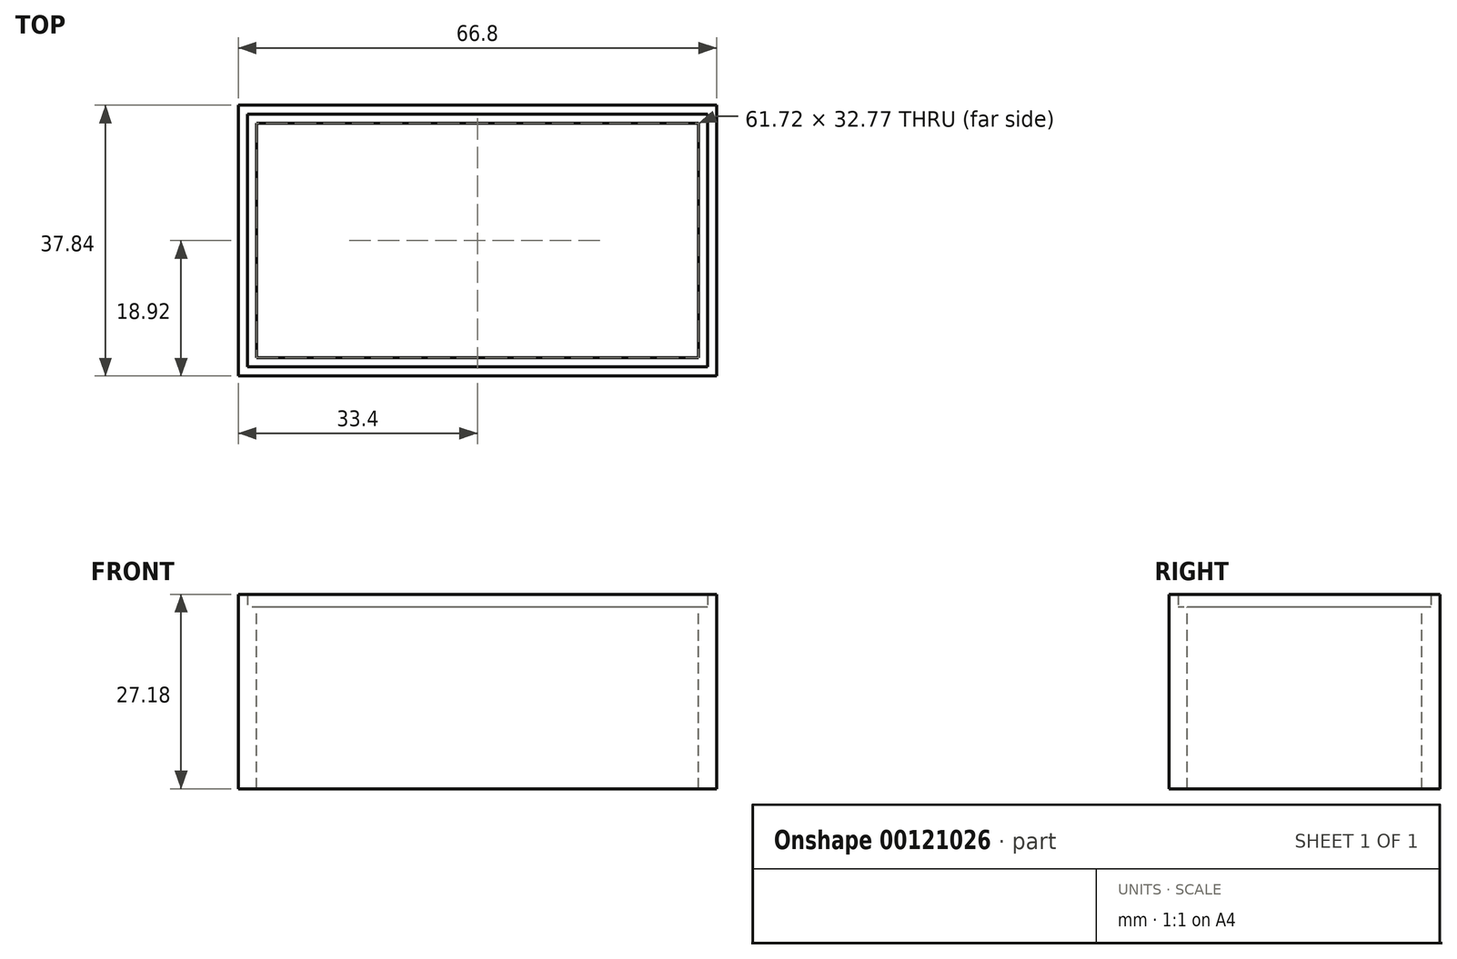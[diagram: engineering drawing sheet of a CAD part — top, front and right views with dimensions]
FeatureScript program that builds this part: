
annotation { "Feature Type Name" : "Feature", "Feature Type Description" : "" }
export const myFeature = defineFeature(function(context is Context, id is Id, definition is map)
    precondition{}
    {
        {
            var Q0;
            Q0=qCreatedBy(makeId("Top.planeOp"),FACE);
            var sketch = newSketch(context, id + "F0", { "sketchPlane" : qUnion([Q0])});
            skLineSegment(sketch, "E0.bottom", {"start": v(32.13, 17.65) * mm, "end": v(-32.13, 17.65) * mm});
            skLineSegment(sketch, "E0.top", {"start": v(32.13, -17.65) * mm, "end": v(-32.13, -17.65) * mm});
            skLineSegment(sketch, "E0.left", {"start": v(32.13, 17.65) * mm, "end": v(32.13, -17.65) * mm});
            skLineSegment(sketch, "E0.right", {"start": v(-32.13, 17.65) * mm, "end": v(-32.13, -17.65) * mm});
            skPoint(sketch, "E0.middle", {"position": v(0, 0) * mm});
            skLineSegment(sketch, "E1.0", {"start": v(30.86, -16.38) * mm, "end": v(-30.86, -16.38) * mm});
            skLineSegment(sketch, "E1.1", {"start": v(30.86, 16.38) * mm, "end": v(30.86, -16.38) * mm});
            skLineSegment(sketch, "E1.2", {"start": v(30.86, 16.38) * mm, "end": v(-30.86, 16.38) * mm});
            skLineSegment(sketch, "E1.3", {"start": v(-30.86, 16.38) * mm, "end": v(-30.86, -16.38) * mm});
            skSolve(sketch);
        }
        {
            var Q0;
            Q0 = qSketchRegion(id + "F0", true);
            extrude(context, id + "F1", {"entities" : qUnion([Q0]), "oppositeDirection" : true, "depth" : 25.4 * mm});
        }
        {
            var Q0;
            Q0=qCreatedBy(makeId("Top.planeOp"),FACE);
            var sketch = newSketch(context, id + "F2", { "sketchPlane" : qUnion([Q0])});
            skLineSegment(sketch, "E2.0", {"start": v(33.4, 18.92) * mm, "end": v(-33.4, 18.92) * mm});
            skLineSegment(sketch, "E2.1", {"start": v(33.4, 18.92) * mm, "end": v(33.4, -18.92) * mm});
            skLineSegment(sketch, "E2.2", {"start": v(33.4, -18.92) * mm, "end": v(-33.4, -18.92) * mm});
            skLineSegment(sketch, "E2.3", {"start": v(-33.4, 18.92) * mm, "end": v(-33.4, -18.92) * mm});
            skLineSegment(sketch, "E3.0", {"start": v(-32.13, 17.65) * mm, "end": v(-32.13, -17.65) * mm});
            skLineSegment(sketch, "E3.1", {"start": v(32.13, -17.65) * mm, "end": v(-32.13, -17.65) * mm});
            skLineSegment(sketch, "E3.2", {"start": v(32.13, 17.65) * mm, "end": v(32.13, -17.65) * mm});
            skLineSegment(sketch, "E3.3", {"start": v(32.13, 17.65) * mm, "end": v(-32.13, 17.65) * mm});
            skSolve(sketch);
        }
        {
            var Q0;
            Q0 = qSketchRegion(id + "F2", true);
            var Q1;
            Q1=makeQuery(id+"F1.opExtrude","CAP_FACE",FACE,{"disambiguationData":[OSD([sQuery(id+"F0.wireOp",EDGE,"E0.bottom"),sQuery(id+"F0.wireOp",EDGE,"E0.top"),sQuery(id+"F0.wireOp",EDGE,"E0.left"),sQuery(id+"F0.wireOp",EDGE,"E0.right"),sQuery(id+"F0.wireOp",EDGE,"E1.0"),sQuery(id+"F0.wireOp",EDGE,"E1.1"),sQuery(id+"F0.wireOp",EDGE,"E1.2"),sQuery(id+"F0.wireOp",EDGE,"E1.3")])],"isStart":false});
            extrude(context, id + "F3", {"entities" : qUnion([Q0]), "operationType" : NewBodyOperationType.ADD, "depth" : 1.78 * mm, "hasSecondDirection" : true, "secondDirectionBound" : SecondDirectionBoundingType.UP_TO_SURFACE, "secondDirectionOppositeDirection" : true, "secondDirectionBoundEntityFace" : qUnion([Q1]), "secondDirectionDepth" : 1.27 * mm});
        }
    });
